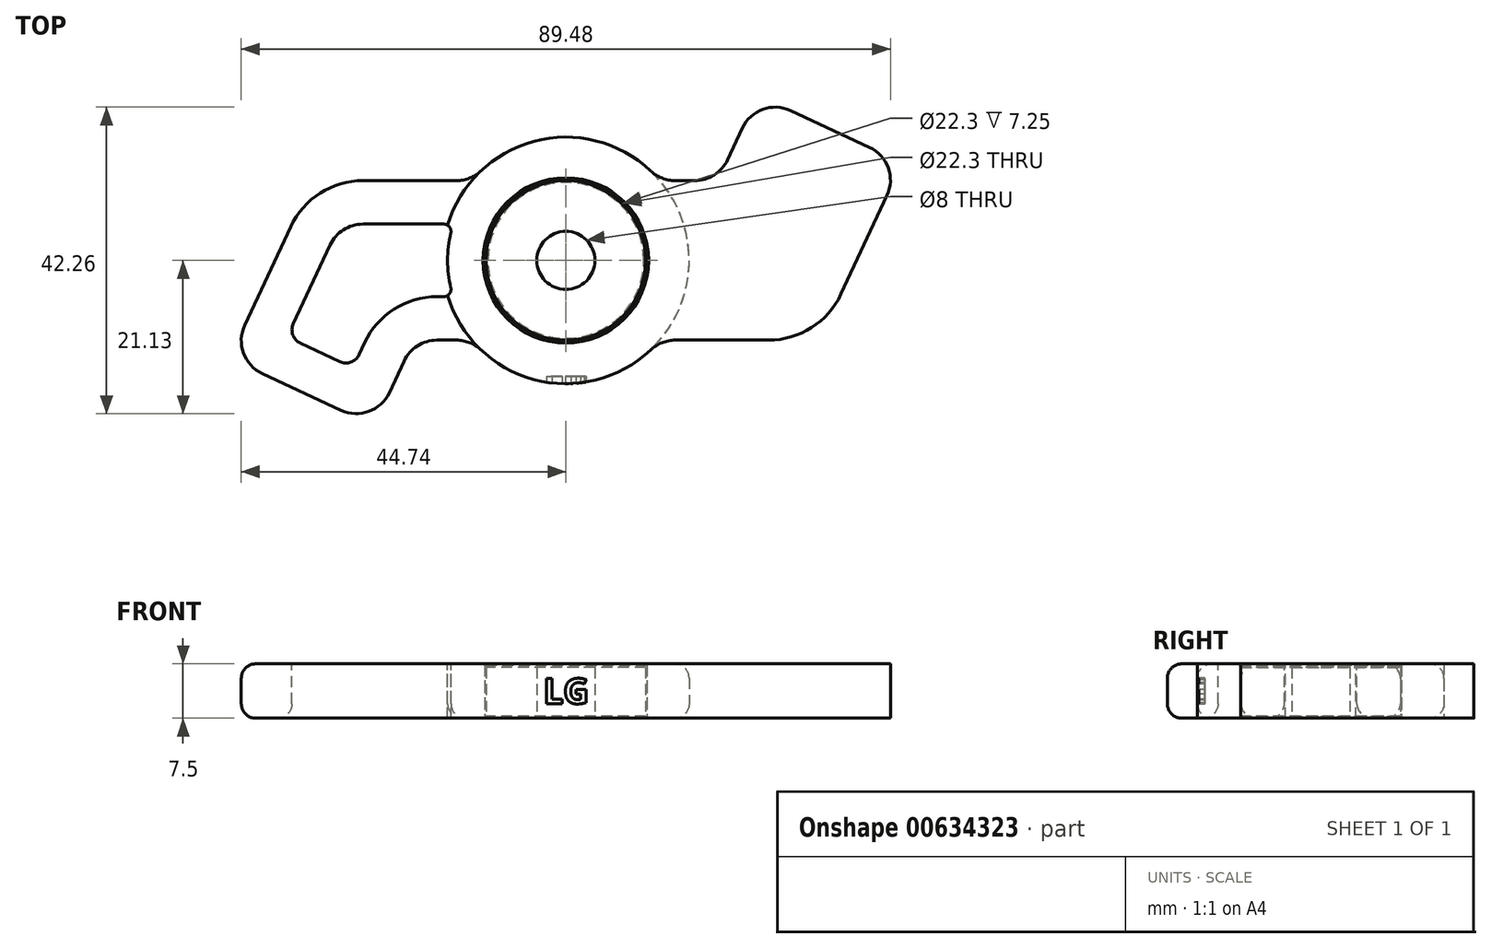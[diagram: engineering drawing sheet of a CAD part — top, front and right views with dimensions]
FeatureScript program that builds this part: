
annotation { "Feature Type Name" : "Feature", "Feature Type Description" : "" }
export const myFeature = defineFeature(function(context is Context, id is Id, definition is map)
    precondition{}
    {
        {
            var Q0;
            Q0=qCreatedBy(makeId("Top.planeOp"),FACE);
            var sketch = newSketch(context, id + "F0", { "sketchPlane" : qUnion([Q0])});
            skCircle(sketch, "E0", {"center": v(0, 0) * mm, "radius": 11 * mm});
            skCircle(sketch, "E1", {"center": v(0, 0) * mm, "radius": 4 * mm});
            skSolve(sketch);
        }
        {
            var Q0;
            Q0=makeQuery(id+"F0.imprint","IMPRINT",FACE,{"disambiguationData":[TD([[makeQuery(id+"F0.imprint","IMPRINT",EDGE,{"derivedFrom":sQuery(id+"F0.wireOp",EDGE,"E0")}),1.0]])]});
            extrude(context, id + "F1", {"entities" : qUnion([Q0]), "depth" : 7 * mm, "offsetDistance" : 25 * mm});
        }
        {
            var Q0;
            Q0=qCreatedBy(makeId("Top.planeOp"),FACE);
            var sketch = newSketch(context, id + "F2", { "sketchPlane" : qUnion([Q0])});
            skLineSegment(sketch, "E2.bottom", {"start": v(-27.96, 11) * mm, "end": v(-15.1, 11) * mm});
            skLineSegment(sketch, "E2.top", {"start": v(-17.77, -11) * mm, "end": v(-15.1, -11) * mm});
            skPoint(sketch, "E2.middle", {"position": v(0, 0) * mm});
            skArc(sketch, "E3.0", {"start": v(-11.67, -12.36) * mm, "mid": v(17, 0) * mm, "end": v(-11.67, 12.36) * mm});
            skPoint(sketch, "E2.right.start.orphan", {"position": v(27.96, 11) * mm});
            skPoint(sketch, "E4.orphan", {"position": v(27.96, -11) * mm});
            skArc(sketch, "E5", {"start": v(-27.96, 11) * mm, "mid": v(-33.87, 9.28) * mm, "end": v(-37.93, 4.65) * mm});
            skLineSegment(sketch, "E6.bottom", {"start": v(-41.85, -15.6) * mm, "end": v(-30.98, -20.66) * mm});
            skLineSegment(sketch, "E6.left", {"start": v(-44.27, -8.95) * mm, "end": v(-37.93, 4.65) * mm});
            skLineSegment(sketch, "E6.right", {"start": v(-24.33, -18.24) * mm, "end": v(-22.3, -13.89) * mm});
            skPoint(sketch, "E7.orphan", {"position": v(-27.96, -11) * mm});
            skPoint(sketch, "E8.visualSharp", {"position": v(-46.38, -13.48) * mm});
            skArc(sketch, "E8.filletArc", {"start": v(-44.27, -8.95) * mm, "mid": v(-44.44, -12.77) * mm, "end": v(-41.85, -15.6) * mm});
            skPoint(sketch, "E9.visualSharp", {"position": v(-26.44, -22.77) * mm});
            skArc(sketch, "E9.filletArc", {"start": v(-30.98, -20.66) * mm, "mid": v(-27.15, -20.83) * mm, "end": v(-24.33, -18.24) * mm});
            skPoint(sketch, "E10.visualSharp", {"position": v(-20.95, -11) * mm});
            skArc(sketch, "E10.filletArc", {"start": v(-17.77, -11) * mm, "mid": v(-20.45, -11.78) * mm, "end": v(-22.3, -13.89) * mm});
            skPoint(sketch, "E11.visualSharp", {"position": v(-12.96, -11) * mm});
            skArc(sketch, "E11.filletArc", {"start": v(-11.67, -12.36) * mm, "mid": v(-13.25, -11.35) * mm, "end": v(-15.1, -11) * mm});
            skPoint(sketch, "E12.visualSharp", {"position": v(-12.96, 11) * mm});
            skArc(sketch, "E12.filletArc", {"start": v(-15.1, 11) * mm, "mid": v(-13.25, 11.35) * mm, "end": v(-11.67, 12.36) * mm});
            skCircle(sketch, "E13.0", {"center": v(0, 0) * mm, "radius": 11.15 * mm});
            skSolve(sketch);
        }
        {
            var Q0;
            Q0=makeQuery(id+"F2.imprint","IMPRINT",FACE,{"disambiguationData":[TD([[makeQuery(id+"F2.imprint","IMPRINT",EDGE,{"derivedFrom":sQuery(id+"F2.wireOp",EDGE,"E2.bottom")}),-1.0]])]});
            extrude(context, id + "F3", {"entities" : qUnion([Q0]), "depth" : 7.5 * mm, "offsetDistance" : 25 * mm});
        }
        {
            var Q0;
            Q0=makeQuery(id+"F3.opExtrude","SWEPT_BODY",BODY,{"disambiguationData":[OSD([sQuery(id+"F2.wireOp",EDGE,"E2.bottom"),sQuery(id+"F2.wireOp",EDGE,"E2.top"),sQuery(id+"F2.wireOp",EDGE,"E3.0"),sQuery(id+"F2.wireOp",EDGE,"E5"),sQuery(id+"F2.wireOp",EDGE,"E6.bottom"),sQuery(id+"F2.wireOp",EDGE,"E6.left"),sQuery(id+"F2.wireOp",EDGE,"E6.right"),sQuery(id+"F2.wireOp",EDGE,"E8.filletArc"),sQuery(id+"F2.wireOp",EDGE,"E9.filletArc"),sQuery(id+"F2.wireOp",EDGE,"E10.filletArc"),sQuery(id+"F2.wireOp",EDGE,"E11.filletArc"),sQuery(id+"F2.wireOp",EDGE,"E12.filletArc"),sQuery(id+"F2.wireOp",EDGE,"E13.0")])]});
            var Q1;
            Q1=makeQuery(id+"F3.opExtrude","CAP_EDGE",EDGE,{"disambiguationData":[OSD([sQuery(id+"F2.wireOp",EDGE,"E13.0")])],"isStart":false});
            circularPattern(context, id + "F4", {"operationType" : NewBodyOperationType.ADD, "entities" : qUnion([Q0]), "axis" : qUnion([Q1]), "angle" : 360 * degree, "instanceCount" : 2, "equalSpace" : true});
        }
        {
            var Q0;
            Q0=makeQuery(id+"F3.opExtrude","CAP_FACE",FACE,{"disambiguationData":[OSD([sQuery(id+"F2.wireOp",EDGE,"E2.bottom"),sQuery(id+"F2.wireOp",EDGE,"E2.top"),sQuery(id+"F2.wireOp",EDGE,"E3.0"),sQuery(id+"F2.wireOp",EDGE,"E5"),sQuery(id+"F2.wireOp",EDGE,"E6.bottom"),sQuery(id+"F2.wireOp",EDGE,"E6.left"),sQuery(id+"F2.wireOp",EDGE,"E6.right"),sQuery(id+"F2.wireOp",EDGE,"E8.filletArc"),sQuery(id+"F2.wireOp",EDGE,"E9.filletArc"),sQuery(id+"F2.wireOp",EDGE,"E10.filletArc"),sQuery(id+"F2.wireOp",EDGE,"E11.filletArc"),sQuery(id+"F2.wireOp",EDGE,"E12.filletArc"),sQuery(id+"F2.wireOp",EDGE,"E13.0")])],"isStart":false});
            var sketch = newSketch(context, id + "F5", { "sketchPlane" : qUnion([Q0])});
            skLineSegment(sketch, "E14.0", {"start": v(-27.96, 5) * mm, "end": v(-16.83, 5) * mm});
            skArc(sketch, "E14.1", {"start": v(-27.96, 5) * mm, "mid": v(-30.65, 4.22) * mm, "end": v(-32.5, 2.11) * mm});
            skLineSegment(sketch, "E14.2", {"start": v(-37.56, -8.76) * mm, "end": v(-32.5, 2.11) * mm});
            skLineSegment(sketch, "E14.3", {"start": v(-17.77, -5) * mm, "end": v(-16.83, -5) * mm});
            skArc(sketch, "E14.4", {"start": v(-17.77, -5) * mm, "mid": v(-23.68, -6.72) * mm, "end": v(-27.74, -11.35) * mm});
            skLineSegment(sketch, "E14.5", {"start": v(-28.5, -12.99) * mm, "end": v(-27.74, -11.35) * mm});
            skLineSegment(sketch, "E14.6", {"start": v(-36.6, -11.42) * mm, "end": v(-31.16, -13.96) * mm});
            skPoint(sketch, "E15.visualSharp", {"position": v(-38.4, -10.58) * mm});
            skArc(sketch, "E15.filletArc", {"start": v(-37.56, -8.76) * mm, "mid": v(-37.63, -10.3) * mm, "end": v(-36.6, -11.42) * mm});
            skPoint(sketch, "E16.visualSharp", {"position": v(-29.35, -14.8) * mm});
            skArc(sketch, "E16.filletArc", {"start": v(-31.16, -13.96) * mm, "mid": v(-29.63, -14.02) * mm, "end": v(-28.5, -12.99) * mm});
            skArc(sketch, "E17.0", {"start": v(-15.86, 3.77) * mm, "mid": v(-16.3, 0) * mm, "end": v(-15.86, -3.77) * mm});
            skPoint(sketch, "E18.visualSharp", {"position": v(-15.51, 5) * mm});
            skArc(sketch, "E18.filletArc", {"start": v(-15.86, 3.77) * mm, "mid": v(-16.05, 4.62) * mm, "end": v(-16.83, 5) * mm});
            skPoint(sketch, "E19.visualSharp", {"position": v(-15.51, -5) * mm});
            skArc(sketch, "E19.filletArc", {"start": v(-16.83, -5) * mm, "mid": v(-16.05, -4.62) * mm, "end": v(-15.86, -3.77) * mm});
            skSolve(sketch);
        }
        {
            var Q0;
            Q0=makeQuery(id+"F5.imprint","IMPRINT",FACE,{"disambiguationData":[TD([[makeQuery(id+"F5.imprint","IMPRINT",EDGE,{"derivedFrom":sQuery(id+"F5.wireOp",EDGE,"E14.0")}),-1.0]])]});
            extrude(context, id + "F6", {"entities" : qUnion([Q0]), "operationType" : NewBodyOperationType.REMOVE, "oppositeDirection" : true, "depth" : 25 * mm, "offsetDistance" : 25 * mm});
        }
        {
            var Q0;
            Q0=makeQuery(id+"F6.boolean.opBoolean","COPY",EDGE,{"derivedFrom":makeQuery(id+"F6.opExtrude","CAP_EDGE",EDGE,{"disambiguationData":[OSD([sQuery(id+"F5.wireOp",EDGE,"E14.0")])],"isStart":true})});
            var Q1;
            {var subQ0=makeQuery(id+"F3.opExtrude","CAP_FACE",FACE,{"disambiguationData":[OSD([sQuery(id+"F2.wireOp",EDGE,"E2.bottom"),sQuery(id+"F2.wireOp",EDGE,"E2.top"),sQuery(id+"F2.wireOp",EDGE,"E3.0"),sQuery(id+"F2.wireOp",EDGE,"E5"),sQuery(id+"F2.wireOp",EDGE,"E6.bottom"),sQuery(id+"F2.wireOp",EDGE,"E6.left"),sQuery(id+"F2.wireOp",EDGE,"E6.right"),sQuery(id+"F2.wireOp",EDGE,"E8.filletArc"),sQuery(id+"F2.wireOp",EDGE,"E9.filletArc"),sQuery(id+"F2.wireOp",EDGE,"E10.filletArc"),sQuery(id+"F2.wireOp",EDGE,"E11.filletArc"),sQuery(id+"F2.wireOp",EDGE,"E12.filletArc"),sQuery(id+"F2.wireOp",EDGE,"E13.0")])],"isStart":true});Q1=makeQuery(id+"F6.boolean.opBoolean","INTERSECT",EDGE,{"derivedFrom":[makeQuery(id+"F4.boolean.opBoolean","MERGE",FACE,{"derivedFrom":[subQ0,makeQuery(id+"F4.opPattern","COPY",FACE,{"derivedFrom":subQ0,"instanceName":"1"})]}),makeQuery(id+"F6.opExtrude","SWEPT_FACE",FACE,{"disambiguationData":[OSD([sQuery(id+"F5.wireOp",EDGE,"E14.6")])]})]});}
            fillet(context, id + "F7", {"entities" : qUnion([Q0, Q1]), "radius" : 2 * mm, "tangentPropagation" : true, "allowEdgeOverflow" : false});
        }
        {
            var Q0;
            {var subQ0=sQuery(id+"F2.wireOp",EDGE,"E12.filletArc");var subQ2=sQuery(id+"F2.wireOp",EDGE,"E3.0");Q0=makeQuery(id+"F4.boolean.opBoolean","SPLIT",EDGE,{"disambiguationData":[TD([makeQuery(id+"F3.opExtrude","SWEPT_FACE",FACE,{"disambiguationData":[OSD([subQ0])]})])],"derivedFrom":makeQuery(id+"F3.opExtrude","CAP_EDGE",EDGE,{"disambiguationData":[OSD([subQ2])],"isStart":true})});}
            var Q1;
            {var subQ0=sQuery(id+"F2.wireOp",EDGE,"E12.filletArc");var subQ2=sQuery(id+"F2.wireOp",EDGE,"E3.0");Q1=makeQuery(id+"F4.boolean.opBoolean","SPLIT",EDGE,{"disambiguationData":[TD([makeQuery(id+"F3.opExtrude","SWEPT_FACE",FACE,{"disambiguationData":[OSD([subQ0])]})])],"derivedFrom":makeQuery(id+"F3.opExtrude","CAP_EDGE",EDGE,{"disambiguationData":[OSD([subQ2])],"isStart":false})});}
            fillet(context, id + "F8", {"entities" : qUnion([Q0, Q1]), "radius" : 2 * mm, "tangentPropagation" : true, "allowEdgeOverflow" : false});
        }
        {
            var Q0;
            Q0=makeQuery(id+"F3.opExtrude","CAP_EDGE",EDGE,{"disambiguationData":[OSD([sQuery(id+"F2.wireOp",EDGE,"E13.0")])],"isStart":false});
            var Q1;
            Q1=makeQuery(id+"F1.opExtrude","CAP_EDGE",EDGE,{"disambiguationData":[OSD([sQuery(id+"F0.wireOp",EDGE,"E0")])],"isStart":true});
            chamfer(context, id + "F9", {"entities" : qUnion([Q0, Q1]), "width" : .25 * mm, "tangentPropagation" : true});
        }
        {
            var Q0;
            Q0=qCreatedBy(makeId("Front.planeOp"),FACE);
            cPlane(context, id + "F10", {"entities" : qUnion([Q0]), "cplaneType" : CPlaneType.OFFSET, "offset" : 25 * mm, "width" : 150 * mm, "height" : 150 * mm});
        }
        {
            var Q0;
            Q0=qCreatedBy(id+"F10.planeOp",FACE);
            var sketch = newSketch(context, id + "F11", { "sketchPlane" : qUnion([Q0])});
            skText(sketch, "E20", { "text": "LG", "fontName": "OpenSans-Bold.ttf"});
            const initialGuessF11  = {"E20": [-0.0031, 0.002, 1, 0, 0.0035]};
            skSetInitialGuess(sketch, initialGuessF11);
            skSolve(sketch);
        }
        {
            var Q0;
            Q0=qSketchRegion(id+"F11",true);
            extrude(context, id + "F12", {"entities" : qUnion([Q0]), "operationType" : NewBodyOperationType.REMOVE, "oppositeDirection" : true, "depth" : 9 * mm, "offsetDistance" : 25 * mm});
        }
    });
